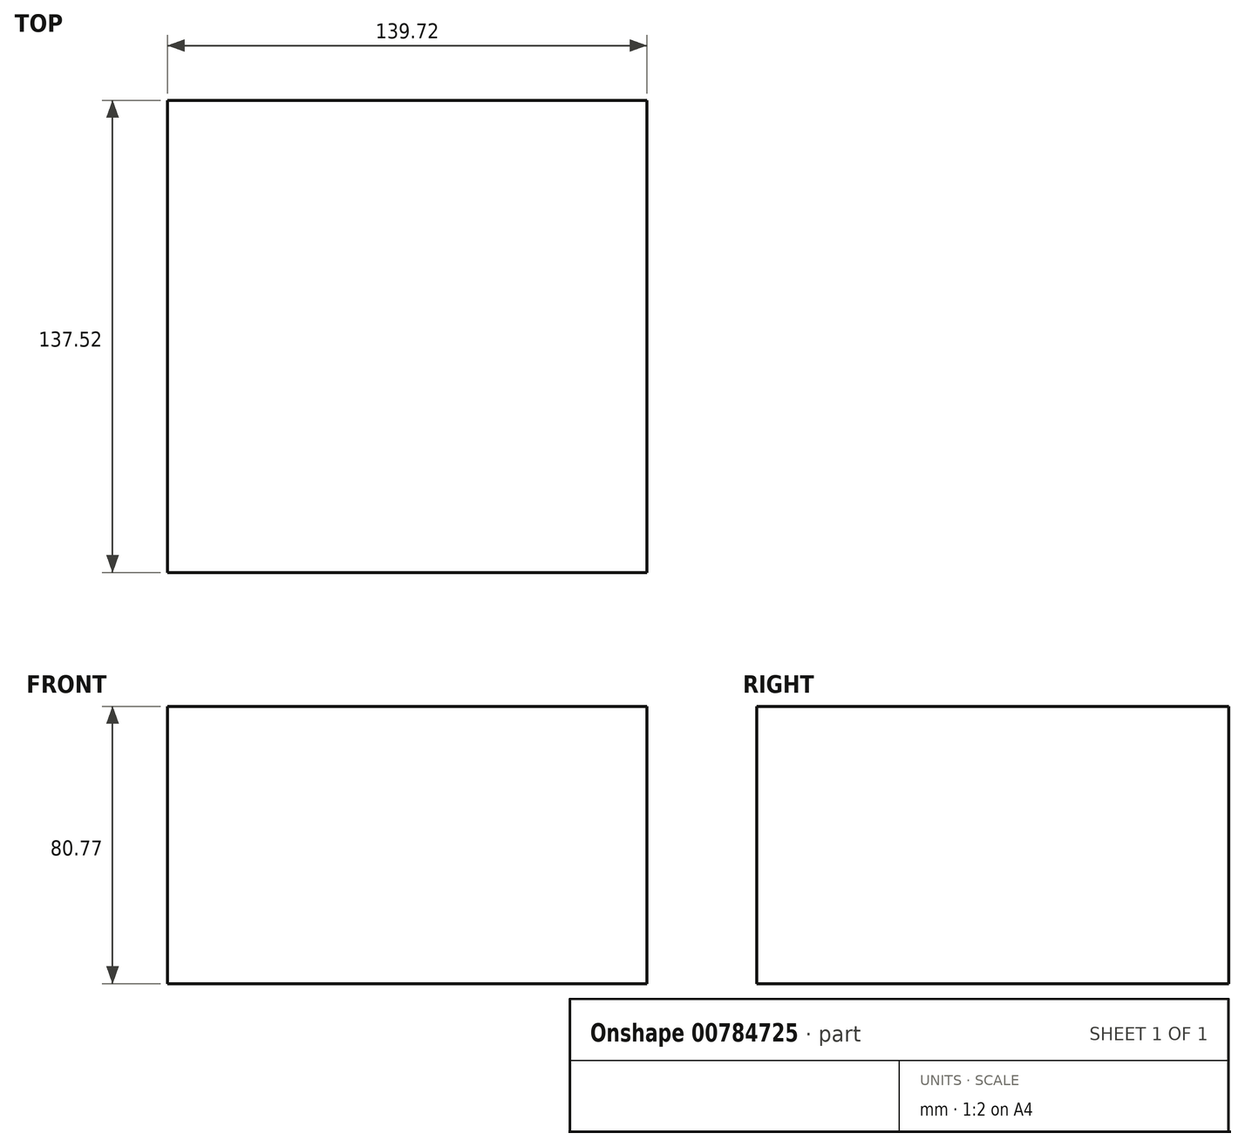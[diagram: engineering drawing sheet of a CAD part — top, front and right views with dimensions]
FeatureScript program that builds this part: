
annotation { "Feature Type Name" : "Feature", "Feature Type Description" : "" }
export const myFeature = defineFeature(function(context is Context, id is Id, definition is map)
    precondition{}
    {
        {
            var Q0;
            Q0=qCreatedBy(makeId("Top.planeOp"),FACE);
            var sketch = newSketch(context, id + "F0", { "sketchPlane" : qUnion([Q0])});
            skLineSegment(sketch, "E0.bottom", {"start": v(69.86, -68.76) * mm, "end": v(-69.86, -68.76) * mm});
            skLineSegment(sketch, "E0.top", {"start": v(69.86, 68.76) * mm, "end": v(-69.86, 68.76) * mm});
            skLineSegment(sketch, "E0.left", {"start": v(69.86, -68.76) * mm, "end": v(69.86, 68.76) * mm});
            skLineSegment(sketch, "E0.right", {"start": v(-69.86, -68.76) * mm, "end": v(-69.86, 68.76) * mm});
            skPoint(sketch, "E0.middle", {"position": v(0, 0) * mm});
            skLineSegment(sketch, "E1", {"start": v(0, 68.76) * mm, "end": v(0, -68.76) * mm});
            skSolve(sketch);
        }
        {
            var Q0;
            Q0=qCreatedBy(makeId("Top.planeOp"),FACE);
            var sketch = newSketch(context, id + "F1", { "sketchPlane" : qUnion([Q0])});
            skCircle(sketch, "E2", {"center": v(54.26, 0) * mm, "radius": 9.82 * mm});
            skSolve(sketch);
        }
        {
            var Q0;
            {var subQ0=sQuery(id+"F0.wireOp",EDGE,"E0.right");Q0=makeQuery(id+"F0.imprint","IMPRINT",FACE,{"disambiguationData":[TD([[makeQuery(id+"F0.imprint","IMPRINT",EDGE,{"derivedFrom":subQ0}),-1.0]])]});}
            var Q1;
            {var subQ0=sQuery(id+"F0.wireOp",EDGE,"E0.left");Q1=makeQuery(id+"F0.imprint","IMPRINT",FACE,{"disambiguationData":[TD([[makeQuery(id+"F0.imprint","IMPRINT",EDGE,{"derivedFrom":subQ0}),1.0]])]});}
            extrude(context, id + "F2", {"entities" : qUnion([Q0, Q1]), "oppositeDirection" : true, "depth" : 80.77 * mm, "offsetDistance" : 25.4 * mm});
        }
        {
            var Q0;
            Q0=sQuery(id+"F1.wireOp",EDGE,"E2");
            var Q1;
            Q1=sQuery(id+"F0.wireOp",EDGE,"E1");
            revolve(context, id + "F3", {"bodyType" : ToolBodyType.SURFACE, "surfaceOperationType" : NewSurfaceOperationType.NEW, "surfaceEntities" : qUnion([Q0]), "axis" : qUnion([Q1]), "revolveType" : RevolveType.FULL});
        }
    });
